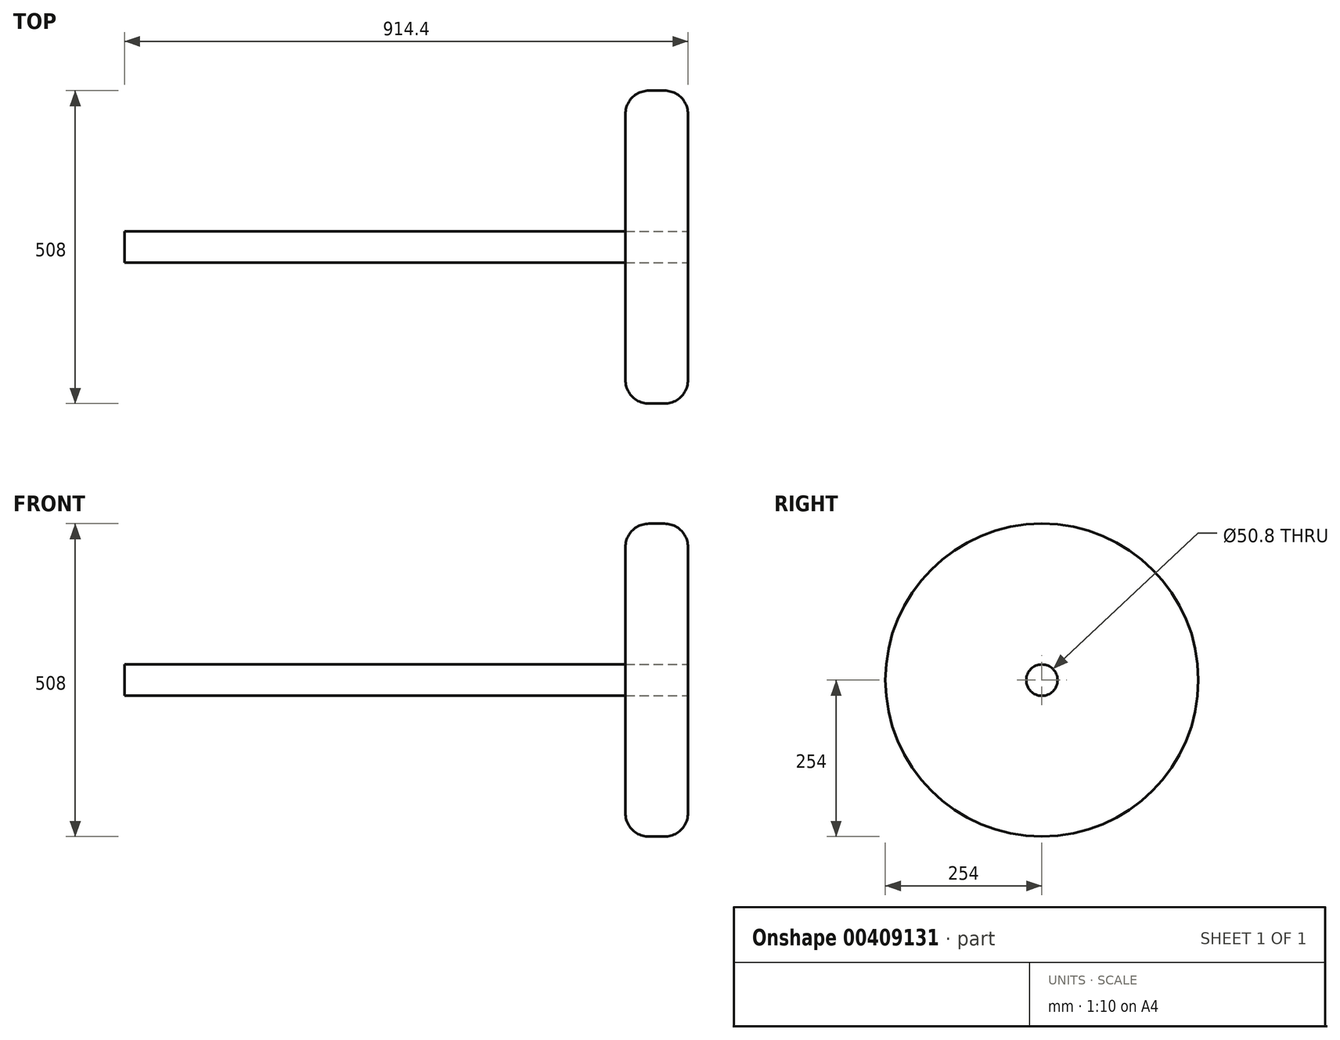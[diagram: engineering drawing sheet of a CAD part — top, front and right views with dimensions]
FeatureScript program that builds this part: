
annotation { "Feature Type Name" : "Feature", "Feature Type Description" : "" }
export const myFeature = defineFeature(function(context is Context, id is Id, definition is map)
    precondition{}
    {
        {
            var Q0;
            Q0=qCreatedBy(makeId("Right.planeOp"),FACE);
            var sketch = newSketch(context, id + "F0", { "sketchPlane" : qUnion([Q0])});
            skCircle(sketch, "E0", {"center": v(0, 0) * mm, "radius": 25.4 * mm});
            skSolve(sketch);
        }
        {
            var Q0;
            Q0=makeQuery(id+"F0.imprint","IMPRINT",FACE,{"disambiguationData":[TD([[makeQuery(id+"F0.imprint","IMPRINT",EDGE,{"derivedFrom":sQuery(id+"F0.wireOp",EDGE,"E0")}),1.0]])]});
            extrude(context, id + "F1", {"entities" : qUnion([Q0]), "endBound" : BoundingType.SYMMETRIC, "depth" : 914.4 * mm});
        }
        {
            var Q0;
            Q0=makeQuery(id+"F1.opExtrude","CAP_FACE",FACE,{"disambiguationData":[OSD([sQuery(id+"F0.wireOp",EDGE,"E0")])],"isStart":false});
            var sketch = newSketch(context, id + "F2", { "sketchPlane" : qUnion([Q0])});
            skCircle(sketch, "E1", {"center": v(0, 0) * mm, "radius": 254 * mm});
            skSolve(sketch);
        }
        {
            var Q0;
            Q0=makeQuery(id+"F2.imprint","IMPRINT",FACE,{"disambiguationData":[TD([[makeQuery(id+"F2.imprint","IMPRINT",EDGE,{"derivedFrom":sQuery(id+"F2.wireOp",EDGE,"E1")}),1.0]])]});
            extrude(context, id + "F3", {"entities" : qUnion([Q0]), "oppositeDirection" : true, "depth" : 101.6 * mm});
        }
        {
            var Q0;
            Q0=makeQuery(id+"F3.opExtrude","CAP_EDGE",EDGE,{"disambiguationData":[OSD([sQuery(id+"F2.wireOp",EDGE,"E1")])],"isStart":true});
            var Q1;
            Q1=makeQuery(id+"F3.opExtrude","CAP_EDGE",EDGE,{"disambiguationData":[OSD([sQuery(id+"F2.wireOp",EDGE,"E1")])],"isStart":false});
            fillet(context, id + "F4", {"entities" : qUnion([Q0, Q1]), "radius" : 38.1 * mm, "tangentPropagation" : true, "allowEdgeOverflow" : false});
        }
    });
